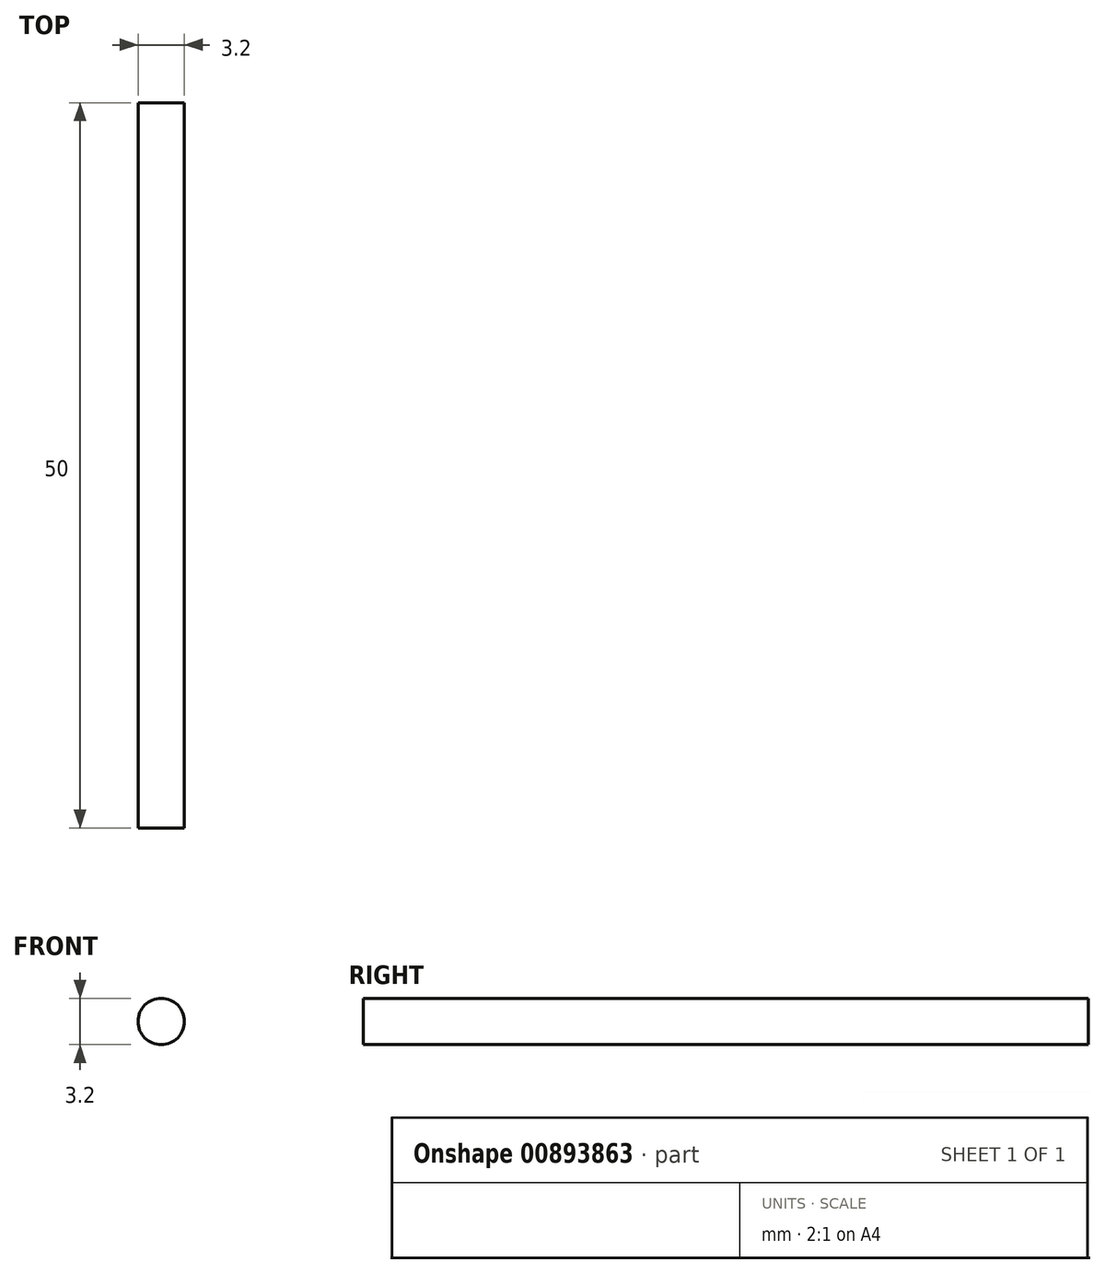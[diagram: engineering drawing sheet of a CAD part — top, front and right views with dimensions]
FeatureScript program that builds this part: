
annotation { "Feature Type Name" : "Feature", "Feature Type Description" : "" }
export const myFeature = defineFeature(function(context is Context, id is Id, definition is map)
    precondition{}
    {
        {
            var Q0;
            Q0=qCreatedBy(makeId("Front.planeOp"),FACE);
            var sketch = newSketch(context, id + "F0", { "sketchPlane" : qUnion([Q0])});
            skCircle(sketch, "E0", {"center": v(0, 0) * mm, "radius": 1.6 * mm});
            skSolve(sketch);
        }
        {
            var Q0;
            Q0 = qSketchRegion(id + "F0", true);
            extrude(context, id + "F1", {"entities" : qUnion([Q0]), "depth" : 50 * mm, "offsetDistance" : 25.4 * mm});
        }
    });
